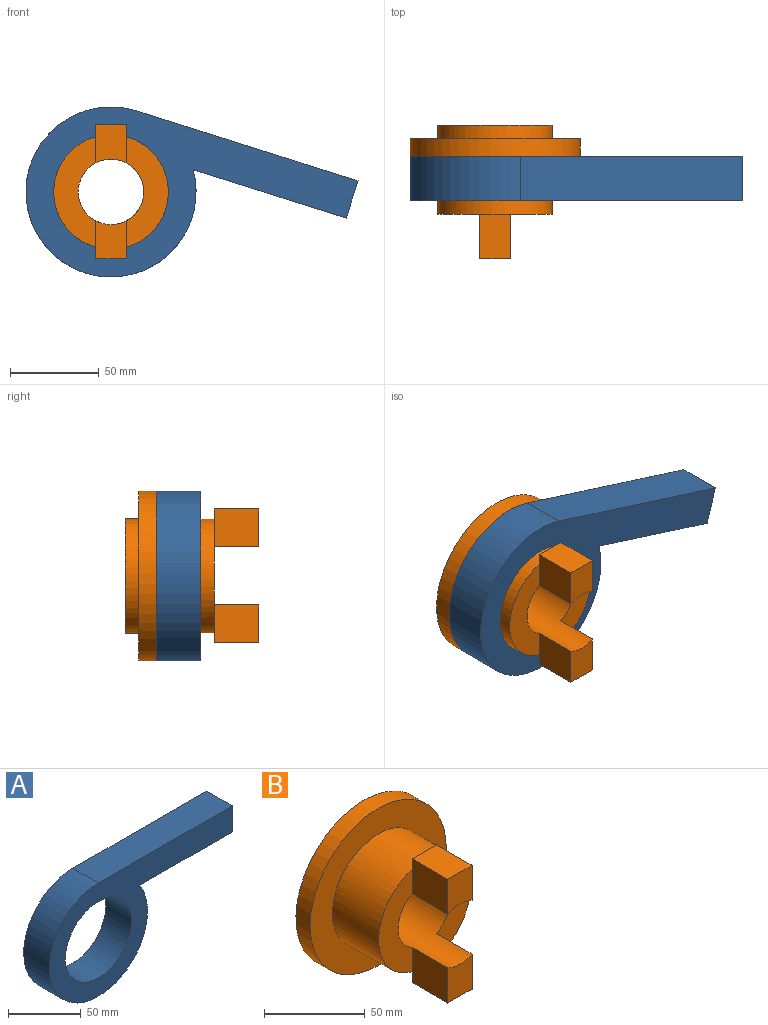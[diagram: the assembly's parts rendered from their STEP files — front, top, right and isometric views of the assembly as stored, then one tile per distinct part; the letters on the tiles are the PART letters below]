
ASSEMBLY  parts=2 mates=1
PART A: 7 faces, bbox 178.3x25x95.6 mm
  f0: cylinder r=47.82mm len=95.64mm, axis (0,1,0), area 6314.1mm2, adj f2,f3,f4,f5
  f1: cylinder r=32.22mm len=64.44mm, axis (0,1,0), area 5061.2mm2, adj f2,f3
  f2: plane 178.33x95.64mm, normal (0,-1,0), area 6174.4mm2, adj f0,f1,f4,f5,f6
  f3: plane 178.33x95.64mm, normal (0,1,0), area 6174.4mm2, adj f0,f1,f4,f5,f6
  f4: plane 130.51x25mm, normal (0,0,1), area 3262.7mm2, adj f0,f2,f3,f6
  f5: plane 90.23x25mm, normal (0,0,-1), area 2255.6mm2, adj f0,f2,f3,f6
  f6: plane 25x22.05mm, normal (1,0,0), area 551.3mm2, adj f2,f3,f4,f5
PART B: 19 faces, bbox 95.6x75x95.6 mm
  f0: plane 62.16x23.72mm, normal (0,-1,0), area 858.4mm2, adj f2,f3,f10,f14
  f1: cylinder r=32.22mm len=64.44mm, axis (0,1,0), area 1518.4mm2, adj f4,f7
  f2: cylinder r=18.41mm len=75mm, axis (0,1,0), area 6667.8mm2, adj f0,f4,f8,f10,f12,f13,f14,f15
  f3: cylinder r=32.22mm len=64.44mm, axis (0,1,0), area 6579.5mm2, adj f0,f6,f8,f9,f18
  f4: plane 64.44x64.44mm, normal (0,1,0), area 2196.5mm2, adj f1,f2
  f5: cylinder r=47.82mm len=95.64mm, axis (0,1,0), area 3004.6mm2, adj f6,f7
  f6: plane 95.64x95.64mm, normal (0,-1,0), area 3922.7mm2, adj f3,f5
  f7: plane 95.64x95.64mm, normal (0,1,0), area 3922.7mm2, adj f1,f5
  f8: plane 62.16x23.72mm, normal (0,-1,0), area 858.4mm2, adj f2,f3,f12,f15
  f9: plane 17x6.57mm, normal (0,1,0), area 98.6mm2, adj f3,f10,f11,f12
  f10: plane 25x21.31mm, normal (1,0,0), area 532.8mm2, adj f0,f2,f9,f11,f13
  f11: plane 25x17mm, normal (0,0,1), area 425mm2, adj f9,f10,f12,f13
  f12: plane 25x21.31mm, normal (-1,0,0), area 532.8mm2, adj f2,f8,f9,f11,f13
  f13: plane 21.31x17mm, normal (0,-1,0), area 338.5mm2, adj f2,f10,f11,f12
  f14: plane 25x21.31mm, normal (1,0,0), area 532.8mm2, adj f0,f2,f16,f17,f18
  f15: plane 25x21.31mm, normal (-1,0,0), area 532.8mm2, adj f2,f8,f16,f17,f18
  f16: plane 25x17mm, normal (0,0,-1), area 425mm2, adj f14,f15,f17,f18
  f17: plane 21.31x17mm, normal (0,-1,0), area 338.5mm2, adj f2,f14,f15,f16
  f18: plane 17x6.57mm, normal (0,1,0), area 98.6mm2, adj f3,f14,f15,f16
PLACE A rot(axis=(0,1,0),17.5deg) t=(0,0,0)mm
PLACE B at identity fixed
MATE revolute A.f1 <-> B.f1  axis (0,1,0) through (0,-5,0)mm
